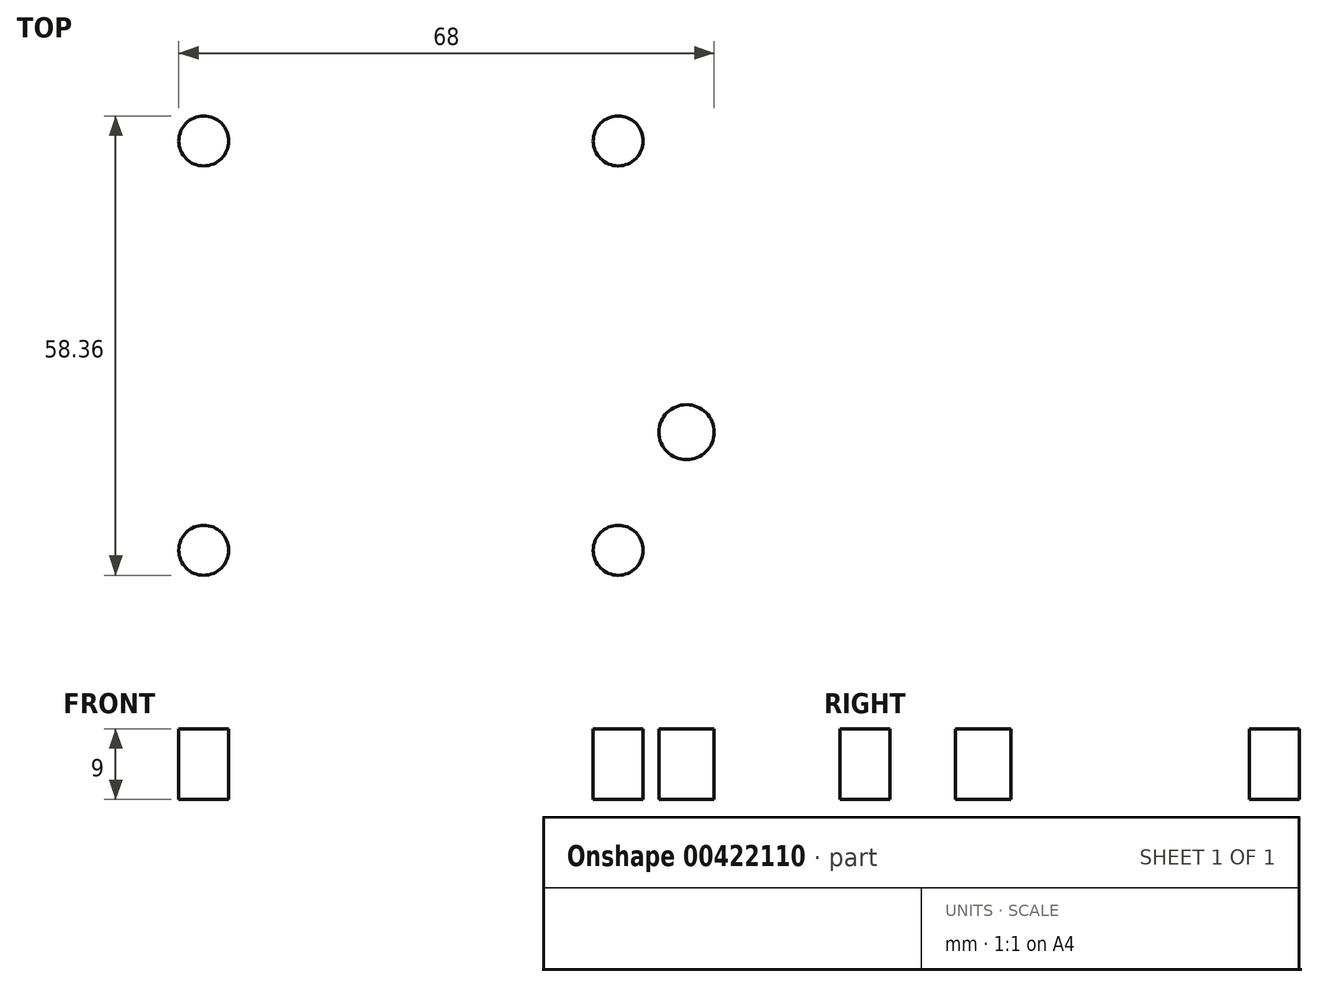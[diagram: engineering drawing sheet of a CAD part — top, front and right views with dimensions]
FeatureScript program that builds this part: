
annotation { "Feature Type Name" : "Feature", "Feature Type Description" : "" }
export const myFeature = defineFeature(function(context is Context, id is Id, definition is map)
    precondition{}
    {
        {
            var Q0;
            Q0=qCreatedBy(makeId("Top.planeOp"),FACE);
            var sketch = newSketch(context, id + "F0", { "sketchPlane" : qUnion([Q0])});
            skLineSegment(sketch, "E0", {"start": v(0, 60) * mm, "end": v(0, -60) * mm});
            skLineSegment(sketch, "E1", {"start": v(-70, 0) * mm, "end": v(70, 0) * mm});
            skLineSegment(sketch, "E2", {"start": v(-31, 37.5) * mm, "end": v(31, 37.5) * mm});
            skLineSegment(sketch, "E3", {"start": v(-31, -37.5) * mm, "end": v(31, -37.5) * mm});
            skCircle(sketch, "E4", {"center": v(-26.32, 26) * mm, "radius": 3.17 * mm});
            skCircle(sketch, "E5", {"center": v(-26.32, -26) * mm, "radius": 3.17 * mm});
            skCircle(sketch, "E6", {"center": v(26.32, -26) * mm, "radius": 3.17 * mm});
            skCircle(sketch, "E7", {"center": v(26.32, 26) * mm, "radius": 3.17 * mm});
            skCircle(sketch, "E8", {"center": v(-41, 0) * mm, "radius": 5.25 * mm});
            skCircle(sketch, "E9", {"center": v(41, 0) * mm, "radius": 5.25 * mm});
            skCircle(sketch, "E10", {"center": v(35, -11) * mm, "radius": 3.5 * mm});
            skLineSegment(sketch, "E11", {"start": v(-55, 12.5) * mm, "end": v(-55, -12.5) * mm});
            skLineSegment(sketch, "E12", {"start": v(55, 12.5) * mm, "end": v(55, -12.5) * mm});
            skLineSegment(sketch, "E13", {"start": v(-40, 28.5) * mm, "end": v(-40, 27.5) * mm});
            skLineSegment(sketch, "E14", {"start": v(40, 28.5) * mm, "end": v(40, 27.5) * mm});
            skLineSegment(sketch, "E15", {"start": v(-40, -27.5) * mm, "end": v(-40, -28.5) * mm});
            skLineSegment(sketch, "E16", {"start": v(40, -27.5) * mm, "end": v(40, -28.5) * mm});
            skArc(sketch, "E17", {"start": v(-54, 13.5) * mm, "mid": v(-44.1, 17.6) * mm, "end": v(-40, 27.5) * mm});
            skArc(sketch, "E18", {"start": v(-40, -27.5) * mm, "mid": v(-44.1, -17.6) * mm, "end": v(-54, -13.5) * mm});
            skArc(sketch, "E19", {"start": v(54, -13.5) * mm, "mid": v(44.1, -17.6) * mm, "end": v(40, -27.5) * mm});
            skArc(sketch, "E20", {"start": v(40, 27.5) * mm, "mid": v(44.1, 17.6) * mm, "end": v(54, 13.5) * mm});
            skArc(sketch, "E21", {"start": v(-54, 13.5) * mm, "mid": v(-54.7, 13.2) * mm, "end": v(-55, 12.5) * mm});
            skArc(sketch, "E22", {"start": v(-55, -12.5) * mm, "mid": v(-54.7, -13.2) * mm, "end": v(-54, -13.5) * mm});
            skArc(sketch, "E23", {"start": v(55, 12.5) * mm, "mid": v(54.7, 13.2) * mm, "end": v(54, 13.5) * mm});
            skArc(sketch, "E24", {"start": v(54, -13.5) * mm, "mid": v(54.7, -13.2) * mm, "end": v(55, -12.5) * mm});
            skArc(sketch, "E25", {"start": v(-31, 37.5) * mm, "mid": v(-37.36, 34.86) * mm, "end": v(-40, 28.5) * mm});
            skArc(sketch, "E26", {"start": v(40, 28.5) * mm, "mid": v(37.36, 34.86) * mm, "end": v(31, 37.5) * mm});
            skArc(sketch, "E27", {"start": v(31, -37.5) * mm, "mid": v(37.36, -34.86) * mm, "end": v(40, -28.5) * mm});
            skArc(sketch, "E28", {"start": v(-40, -28.5) * mm, "mid": v(-37.36, -34.86) * mm, "end": v(-31, -37.5) * mm});
            skCircle(sketch, "E29", {"center": v(0, 0) * mm, "radius": 26 * mm});
            skCircle(sketch, "E30", {"center": v(35, -11) * mm, "radius": 6 * mm});
            skSolve(sketch);
        }
        {
            var Q0;
            Q0=makeQuery(id+"F0.imprint","IMPRINT",FACE,{"disambiguationData":[TD([[makeQuery(id+"F0.imprint","IMPRINT",EDGE,{"derivedFrom":sQuery(id+"F0.wireOp",EDGE,"E4")}),1.0]])]});
            var Q1;
            Q1=makeQuery(id+"F0.imprint","IMPRINT",FACE,{"disambiguationData":[TD([[makeQuery(id+"F0.imprint","IMPRINT",EDGE,{"derivedFrom":sQuery(id+"F0.wireOp",EDGE,"E7")}),1.0]])]});
            var Q2;
            Q2=makeQuery(id+"F0.imprint","IMPRINT",FACE,{"disambiguationData":[TD([[makeQuery(id+"F0.imprint","IMPRINT",EDGE,{"derivedFrom":sQuery(id+"F0.wireOp",EDGE,"E5")}),1.0]])]});
            var Q3;
            Q3=makeQuery(id+"F0.imprint","IMPRINT",FACE,{"disambiguationData":[TD([[makeQuery(id+"F0.imprint","IMPRINT",EDGE,{"derivedFrom":sQuery(id+"F0.wireOp",EDGE,"E6")}),1.0]])]});
            var Q4;
            Q4=makeQuery(id+"F0.imprint","IMPRINT",FACE,{"disambiguationData":[TD([[makeQuery(id+"F0.imprint","IMPRINT",EDGE,{"derivedFrom":sQuery(id+"F0.wireOp",EDGE,"E10")}),1.0]])]});
            extrude(context, id + "F1", {"entities" : qUnion([Q0, Q1, Q2, Q3, Q4]), "depth" : 9 * mm});
        }
    });
